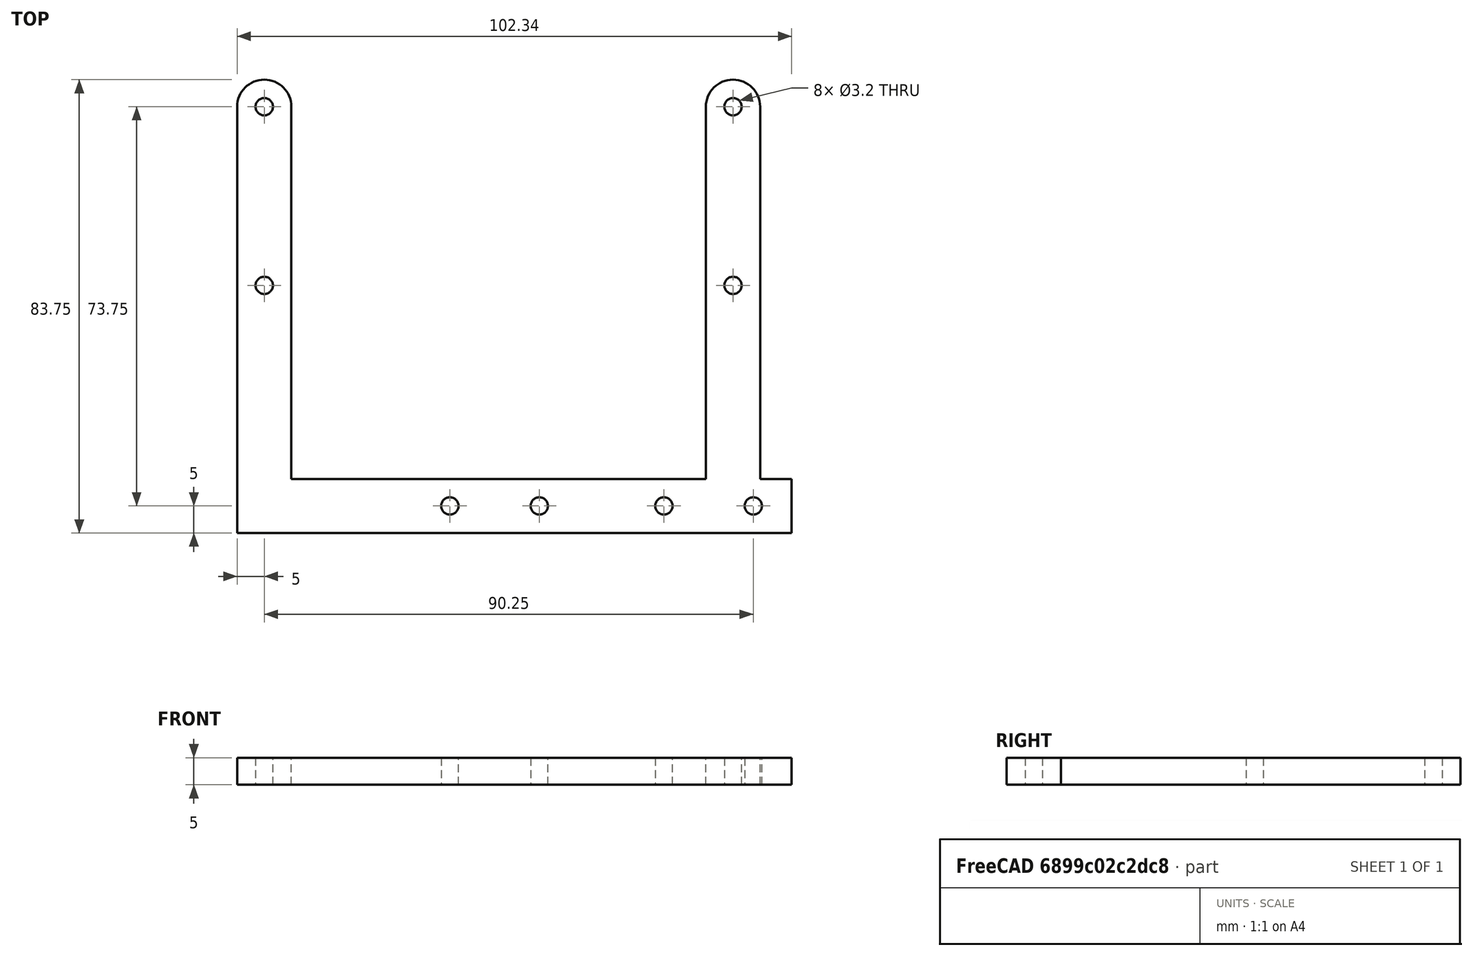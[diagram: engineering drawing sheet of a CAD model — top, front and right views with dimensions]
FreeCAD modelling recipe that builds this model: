
FCSTD DOCUMENT  (FreeCAD 0.20R29177 (Git))
Label: TransmissionEngineHolderConnector
License: All rights reserved
LicenseURL: http://en.wikipedia.org/wiki/All_rights_reserved
objects: Sketcher::SketchObject×1, Spreadsheet::Sheet×1, PartDesign::Pad×1, PartDesign::Body×1
note: 4 computed .brp shape members not serialized (recipe doc carries the construction recipe); baked Part::Feature solids carry a one-line shape summary decoded from their .brp

FEATURE [Sketcher::SketchObject] Sketch
  FullyConstrained = false
  MapMode = 5
  Support = -> [XY_Plane]
  expr: Constraints[10] = Spreadsheet.transmissionScrewBottomY
  expr: Constraints[11] = Spreadsheet.transmissionScrewBottomY
  expr: Constraints[15] = Spreadsheet.sideArmThickness
  expr: Constraints[29] = Spreadsheet.sideArmThickness * 2
  expr: Constraints[30] = Spreadsheet.sideArmThickness * 2
  expr: Constraints[34] = Spreadsheet.screwR
  expr: Constraints[35] = Spreadsheet.bottomScrew1X - Spreadsheet.engineShaftX
  expr: Constraints[36] = Spreadsheet.bottomScrew1X + Spreadsheet.engineShaftX
  expr: Constraints[37] = Spreadsheet.bottomScrew2X - Spreadsheet.engineShaftX
  expr: Constraints[38] = Spreadsheet.bottomScrew2X + Spreadsheet.engineShaftX
  expr: Constraints[3] = Spreadsheet.screwR
  expr: Constraints[40] = Spreadsheet.engineShaftToScrewY
  expr: Constraints[45] = Spreadsheet.sideArmThickness
  expr: Constraints[46] = Spreadsheet.sideArmThickness
  expr: Constraints[4] = Spreadsheet.transmssionScrewXOrig
  expr: Constraints[5] = Spreadsheet.transmssionScrewXOrig
  expr: Constraints[6] = Spreadsheet.transmssionScrewXOrig
  expr: Constraints[7] = Spreadsheet.transmssionScrewXOrig
  expr: Constraints[8] = Spreadsheet.transmissionScrewTopY
  expr: Constraints[9] = Spreadsheet.transmissionScrewTopY
  sketch-geometry (19):
    g0: Circle CenterX=-43.25 CenterY=7.75 CenterZ=0 NormalX=0 NormalY=0 NormalZ=1 AngleXU=0 Radius=1.6
    g1: Circle CenterX=43.25 CenterY=7.75 CenterZ=0 NormalX=0 NormalY=0 NormalZ=1 AngleXU=0 Radius=1.6
    g2: Circle CenterX=-43.25 CenterY=-25.25 CenterZ=0 NormalX=0 NormalY=0 NormalZ=1 AngleXU=0 Radius=1.6
    g3: Circle CenterX=43.25 CenterY=-25.25 CenterZ=0 NormalX=0 NormalY=0 NormalZ=1 AngleXU=0 Radius=1.6
    g4: ArcOfCircle CenterX=-43.25 CenterY=7.75 CenterZ=0 NormalX=0 NormalY=0 NormalZ=1 AngleXU=0 Radius=5 StartAngle=3.57506e-08 EndAngle=3.14159
    g5: ArcOfCircle CenterX=43.25 CenterY=7.75 CenterZ=0 NormalX=0 NormalY=0 NormalZ=1 AngleXU=0 Radius=5 StartAngle=6.28319 EndAngle=9.42478
    g6: LineSegment StartX=-48.25 StartY=7.75 StartZ=0 EndX=-48.25 EndY=-71 EndZ=0
    g7: LineSegment StartX=-48.25 StartY=-71 StartZ=0 EndX=54.0881 EndY=-71 EndZ=0
    g8: LineSegment StartX=48.25 StartY=7.75 StartZ=0 EndX=48.25 EndY=-61 EndZ=0
    g9: LineSegment StartX=-38.25 StartY=7.75 StartZ=0 EndX=-38.25 EndY=-61 EndZ=0
    g10: LineSegment StartX=-38.25 StartY=-61 StartZ=0 EndX=38.25 EndY=-61 EndZ=0
    g11: LineSegment StartX=38.25 StartY=7.75 StartZ=0 EndX=38.25 EndY=-61 EndZ=0
    g12: Circle CenterX=7.5 CenterY=-66 CenterZ=0 NormalX=0 NormalY=0 NormalZ=1 AngleXU=0 Radius=1.6
    g13: Circle CenterX=-9 CenterY=-66 CenterZ=0 NormalX=0 NormalY=0 NormalZ=1 AngleXU=0 Radius=1.6
    g14: Circle CenterX=30.5 CenterY=-66 CenterZ=0 NormalX=0 NormalY=0 NormalZ=1 AngleXU=0 Radius=1.6
    g15: Circle CenterX=47 CenterY=-66 CenterZ=0 NormalX=0 NormalY=0 NormalZ=1 AngleXU=0 Radius=1.6
    g16: LineSegment StartX=-113.479 StartY=-66 StartZ=0 EndX=44.3691 EndY=-66 EndZ=0
    g17: LineSegment StartX=48.25 StartY=-61 StartZ=0 EndX=54.0881 EndY=-61 EndZ=0
    g18: LineSegment StartX=54.0881 StartY=-61 StartZ=0 EndX=54.0881 EndY=-71 EndZ=0
  constraints (53):
    c: Equal(g0,g1)
    c: Equal(g0,g2)
    c: Equal(g0,g3)
    c: Radius(g0) = 1.6
    c: DistanceX(g-1,g1) = 43.25
    c: DistanceX(g-1,g3) = 43.25
    c: DistanceX(g2,g-1) = 43.25
    c: DistanceX(g0,g-1) = 43.25
    c: DistanceY(g-1,g1) = 7.75
    c: DistanceY(g-1,g0) = 7.75
    c: DistanceY(g3,g-1) = 25.25
    c: DistanceY(g2,g-1) = 25.25
    c: Coincident(g4,g0)
    c: Coincident(g5,g1)
    c: Equal(g4,g5)
    c: Radius(g4) = 5
    c: Vertical(g6)
    c: Coincident(g7,g6)
    c: Horizontal(g7)
    c: Vertical(g8)
    c: Vertical(g9)
    c: Coincident(g10,g9)
    c: Horizontal(g10)
    c: Vertical(g11)
    c: Coincident(g10,g11)
    c: Coincident(g4,g6)
    c: Coincident(g4,g9)
    c: Tangent(g5,g11) = -1.5708
    c: Coincident(g5,g8)
    c: DistanceX(g4,g4) = 10
    c: DistanceX(g5,g5) = 10
    c: Equal(g12,g13)
    c: Equal(g12,g14)
    c: Equal(g12,g15)
    c: Radius(g12) = 1.6
    c: DistanceX(g12,g-1) = -7.5
    c: DistanceX(g-1,g14) = 30.5
    c: DistanceX(g13,g-1) = 9
    c: DistanceX(g-1,g15) = 47
    c: Horizontal(g16)
    c: DistanceY(g16,g-1) = 66
    c: PointOnObject(g13,g16)
    c: PointOnObject(g12,g16)
    c: PointOnObject(g14,g16)
    c: PointOnObject(g15,g16)
    c: DistanceY(g16,g9) = 5
    c: DistanceY(g6,g13) = 5
    c: DistanceY(g8,g10) = 0
    c: Coincident(g17,g8)
    c: Horizontal(g17)
    c: Coincident(g18,g17)
    c: Vertical(g18)
    c: Coincident(g7,g18)
FEATURE [Spreadsheet::Sheet] Spreadsheet
  cells = A2=engineShaftX; B2(engineShaftX)=19; A3=engineShaftToScrewY; B3(engineShaftToScrewY)=66; A4=bottomScrew1X; B4(bottomScrew1X)=11.5; A5=bottomScrew2X; B5(bottomScrew2X)=28; A6=transmissionScrewTopY; B6(transmissionScrewTopY)=7.75; A7=transmissionScrewBottomY; B7(transmissionScrewBottomY)=25.25; A8=transmssionScrewXOrig; B8(transmssionScrewXOrig)=43.25; A9=screwR; B9(screwR)=1.6; A10=thickness; B10(thickness)=5; A11=sideArmThickness; B11(sideArmThickness)=5; A12=bottomWidth; B12(bottomWidth)=94.34
FEATURE [PartDesign::Pad] Pad
  Direction = (0,0,1)
  Length = 5
  Length2 = 10
  Profile = -> Sketch
  ReferenceAxis = -> Sketch [N_Axis]
  Type = 0
  expr: Length = Spreadsheet.thickness
FEATURE [PartDesign::Body] Body
  Group = -> [Sketch,Pad]
  Origin = -> Origin
  Tip = -> Pad
